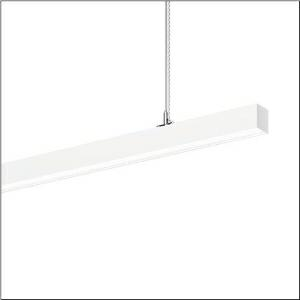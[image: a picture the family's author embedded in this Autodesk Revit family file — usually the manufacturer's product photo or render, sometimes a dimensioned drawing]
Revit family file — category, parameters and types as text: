
# Revit family: silica_r__21_51mx30db45wb_134d
name_source: partatom
category: Lighting Fixtures
units: mm (PartAtom-declared; Revit-internal decimal feet)

## family parameters
Cut with Voids When Loaded = No
Host = Face
Light Source = No
Part Type = Normal
Room Calculation Point = No
Round Connector Dimension = Use Diameter
Shared = No

## types (1)
- --- (1 x LED, 5260 lm, 32 W, 4000K)
    Apparent Load = 32 VA
    CIE Flux Codes = 47 79 96 57 100
    Color Rendering = 80
    Color Temperature = 4000K
    Default Elevation = 1800 mm
    Description = Silica® 21, office luminaire, primary optical cover: cover, of PMMA, opal, light emission: direct/indirect distribution, primary light characteristic: symmetric, installation type: suspended mounting, LED, rated luminous flux: 5.260lm, luminous efficacy: 164lm/W, light colour: 840, colour temperature: 4000K, with terminal, 3+2-pole, max. 2.5mm², mains connection: 220..240V, AC, 50/60Hz, rated input power: 32W, luminaire housing, of aluminium, traffic white (RAL 9016), length: 1.504mm, width: 53mm, height: 53mm, protection rating (complete): IP20, insulation class (complete): insulation class I (protective earthing), certification: CE, permissible operating ambient temperature: 0..+35°C, standard: EN 50419, packaging unit: 1 piece
    Height = 53 mm
    Lamp = 1 x LED
    Lamp Light Flux = 5260 lm
    Lamp Power = 32 W
    Lamp count = 1
    Length = 1504 mm
    Luminous efficacy = 164 lm/W
    Manufacturer = Siteco
    ModVariant = No
    Model = 51MX30DB45WB
    Mounting Place = Ceiling
    Mounting Type = Pendant
    Number of Poles = 1
    OnlyDefault = Yes
    Power Factor = 1
    Product Name = Silica® 21
    Product group = office luminaire | ceiling pendant
    ProductGroupID = 905
    Protection Class = Protection class I
    Protection Degree = IP 20
    RLX_Detail_Level = 1
    RlxData = <blob elided: 21349 chars, md5=6ed53a79>
    Socket = socket
    Standby Power = 0 W
    System Light Flux = 5260 lm
    System Power = 32 W
    Type Comments = factory setting: luminous flux: 100 % | dim-lin: 254 | 218 mA
    Type Image = l_1251642.jpg
    URL = http://relux.com
    VarID = @adj_025213
    Voltage = 0 V
    Weight = 0.00 kg
    Width = 53 mm

## geometry (parser evidence)
native form markers: Blend x4, Sweep x11
no freeform markers — native parametric forms only
